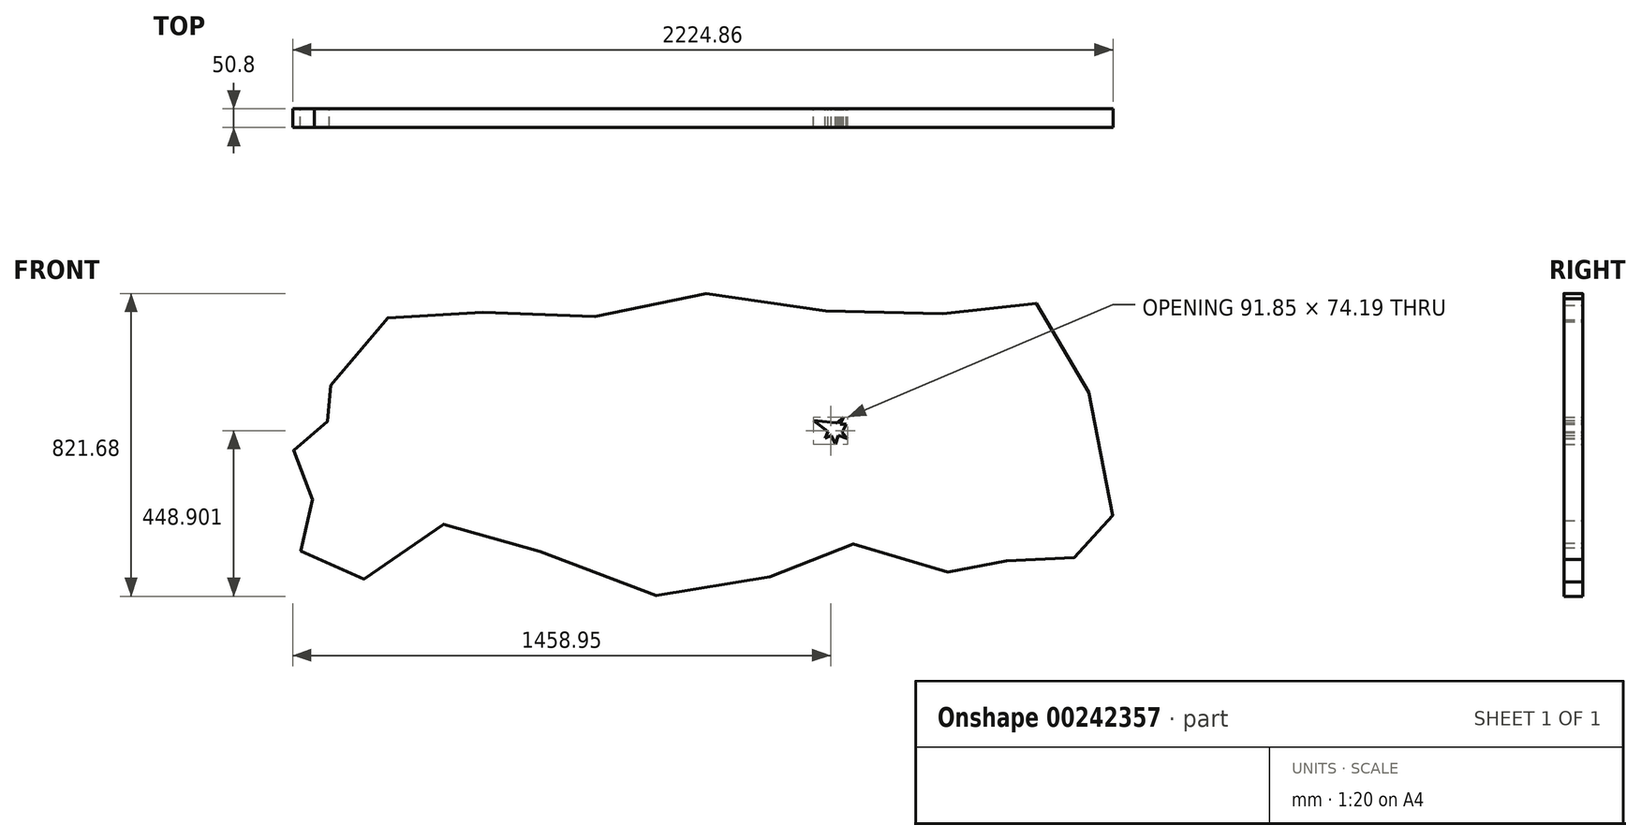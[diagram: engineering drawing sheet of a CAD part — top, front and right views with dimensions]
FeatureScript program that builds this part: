
annotation { "Feature Type Name" : "Feature", "Feature Type Description" : "" }
export const myFeature = defineFeature(function(context is Context, id is Id, definition is map)
    precondition{}
    {
        {
            var Q0;
            Q0=qCreatedBy(makeId("Front.planeOp"),FACE);
            var sketch = newSketch(context, id + "F0", { "sketchPlane" : qUnion([Q0])});
            skLineSegment(sketch, "E0.bottom", {"start": v(0, 0) * mm, "end": v(2286, 0) * mm});
            skLineSegment(sketch, "E0.top", {"start": v(0, 914.4) * mm, "end": v(2286, 914.4) * mm});
            skLineSegment(sketch, "E0.left", {"start": v(0, 0) * mm, "end": v(0, 914.4) * mm});
            skLineSegment(sketch, "E0.right", {"start": v(2286, 0) * mm, "end": v(2286, 914.4) * mm});
            skPoint(sketch, "E1.18.internal.snap0", {"position": v(2286, 457.2) * mm});
            skFitSpline(sketch, "E1", {"points": [v(144.07, 618.65) * mm, v(335.9, 822.65) * mm, v(731.71, 792.2) * mm, v(1188.43, 868.33) * mm, v(1709.09, 798.3) * mm, v(2059.24, 840.92) * mm, v(2241.92, 423.79) * mm, v(2226.7, 149.76) * mm, v(2010.52, 174.12) * mm, v(1931.36, 88.86) * mm, v(1629.92, 186.3) * mm, v(1377.2, 116.27) * mm, v(908.31, 70.6) * mm, v(479, 250.24) * mm, v(208.01, 85.82) * mm, v(61.86, 177.16) * mm, v(98.4, 286.77) * mm, v(64.9, 356.8) * mm, v(52.73, 457.2) * mm, v(141.03, 506) * mm, v(101.44, 560.8) * mm, v(144.07, 618.65) * mm]});
            skCircle(sketch, "E2", {"center": v(1514.7, 499.38) * mm, "radius": 18.14 * mm});
            skLineSegment(sketch, "E3", {"start": v(1518.35, 517.16) * mm, "end": v(1534.76, 532.67) * mm});
            skLineSegment(sketch, "E4", {"start": v(1534.76, 532.67) * mm, "end": v(1526.55, 513.12) * mm});
            skPoint(sketch, "E4.endSnap0", {"position": v(1526.55, 524.91) * mm});
            skLineSegment(sketch, "E5", {"start": v(1526.55, 513.12) * mm, "end": v(1542.73, 513.12) * mm});
            skLineSegment(sketch, "E6", {"start": v(1542.73, 513.12) * mm, "end": v(1530.66, 490.77) * mm});
            skLineSegment(sketch, "E7", {"start": v(1530.66, 490.77) * mm, "end": v(1546.2, 474.33) * mm});
            skLineSegment(sketch, "E8", {"start": v(1546.2, 474.33) * mm, "end": v(1521.47, 482.55) * mm});
            skPoint(sketch, "E8.endSnap0", {"position": v(1538.43, 482.55) * mm});
            skLineSegment(sketch, "E9", {"start": v(1521.47, 482.55) * mm, "end": v(1513.47, 458.47) * mm});
            skLineSegment(sketch, "E10", {"start": v(1513.47, 458.47) * mm, "end": v(1502.45, 482.55) * mm});
            skLineSegment(sketch, "E11", {"start": v(1502.45, 482.55) * mm, "end": v(1485.75, 474.9) * mm});
            skLineSegment(sketch, "E12", {"start": v(1485.75, 474.9) * mm, "end": v(1492.94, 493.46) * mm});
            skLineSegment(sketch, "E13", {"start": v(1492.94, 493.46) * mm, "end": v(1454.34, 524.03) * mm});
            skLineSegment(sketch, "E14", {"start": v(1454.34, 524.03) * mm, "end": v(1502.45, 518.93) * mm});
            skLineSegment(sketch, "E15", {"start": v(1502.45, 518.93) * mm, "end": v(1518.35, 517.16) * mm});
            skSolve(sketch);
        }
        {
            var Q0;
            Q0=makeQuery(id+"F0.imprint","IMPRINT",FACE,{"disambiguationData":[TD([[makeQuery(id+"F0.imprint","IMPRINT",EDGE,{"derivedFrom":sQuery(id+"F0.wireOp",EDGE,"E1")}),-1.0]])]});
            extrude(context, id + "F1", {"entities" : qUnion([Q0]), "depth" : 50.8 * mm});
        }
    });
